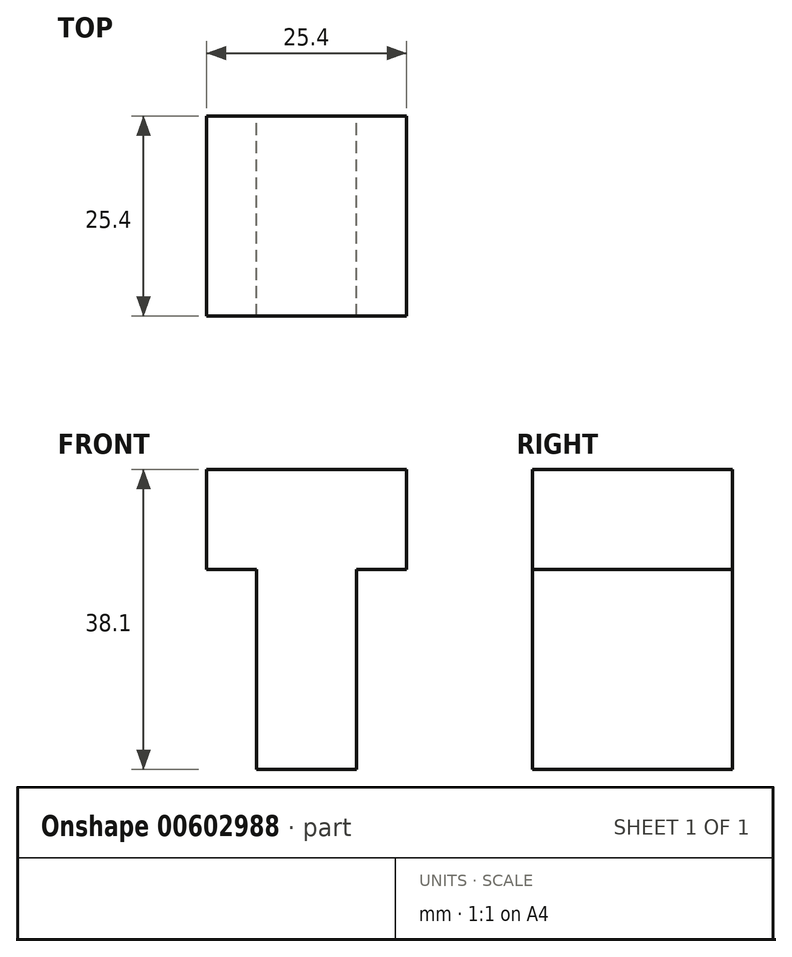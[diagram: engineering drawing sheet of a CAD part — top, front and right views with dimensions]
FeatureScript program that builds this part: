
annotation { "Feature Type Name" : "Feature", "Feature Type Description" : "" }
export const myFeature = defineFeature(function(context is Context, id is Id, definition is map)
    precondition{}
    {
        {
            var Q0;
            Q0=qCreatedBy(makeId("Front.planeOp"),FACE);
            var sketch = newSketch(context, id + "F0", { "sketchPlane" : qUnion([Q0])});
            skLineSegment(sketch, "E0", {"start": v(-18.12, 24.8) * mm, "end": v(7.28, 24.8) * mm});
            skLineSegment(sketch, "E1", {"start": v(7.28, 24.8) * mm, "end": v(7.28, 12.1) * mm});
            skLineSegment(sketch, "E2", {"start": v(7.28, 12.1) * mm, "end": v(0.93, 12.1) * mm});
            skLineSegment(sketch, "E3", {"start": v(0.93, 12.1) * mm, "end": v(0.93, -13.3) * mm});
            skLineSegment(sketch, "E4", {"start": v(0.93, -13.3) * mm, "end": v(-11.77, -13.3) * mm});
            skLineSegment(sketch, "E5", {"start": v(-11.77, -13.3) * mm, "end": v(-11.77, 12.1) * mm});
            skLineSegment(sketch, "E6", {"start": v(-11.77, 12.1) * mm, "end": v(-18.12, 12.1) * mm});
            skLineSegment(sketch, "E7", {"start": v(-18.12, 12.1) * mm, "end": v(-18.12, 24.8) * mm});
            skSolve(sketch);
        }
        {
            var Q0;
            Q0 = qSketchRegion(id + "F0", true);
            extrude(context, id + "F1", {"entities" : qUnion([Q0]), "depth" : 25.4 * mm, "offsetDistance" : 25.4 * mm});
        }
    });
